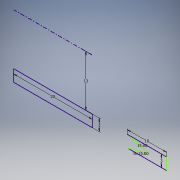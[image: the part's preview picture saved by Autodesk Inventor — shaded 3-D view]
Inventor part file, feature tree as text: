
AUTODESK INVENTOR PART (.ipt)
format: ipt  version: 2019 (Build 230136000, 136)  size: 94,720 bytes
history: native  units: in
note: dims shown in document units (in); Inventor stores cm internally (conversion verified against a paired STEP export)
features: sketch x1
ambient origin geometry x8: Origin, YZ Plane, XZ Plane, XY Plane, X Axis, Y Axis, Z Axis, Center Point
feature tree (1):
  sketch  "Sketch1"  dims[d0=0.7874in d1=0.1181in d2=0.5118in d3=0.3937in d4=15.0deg d5=15.0deg d6=0.1181in]
